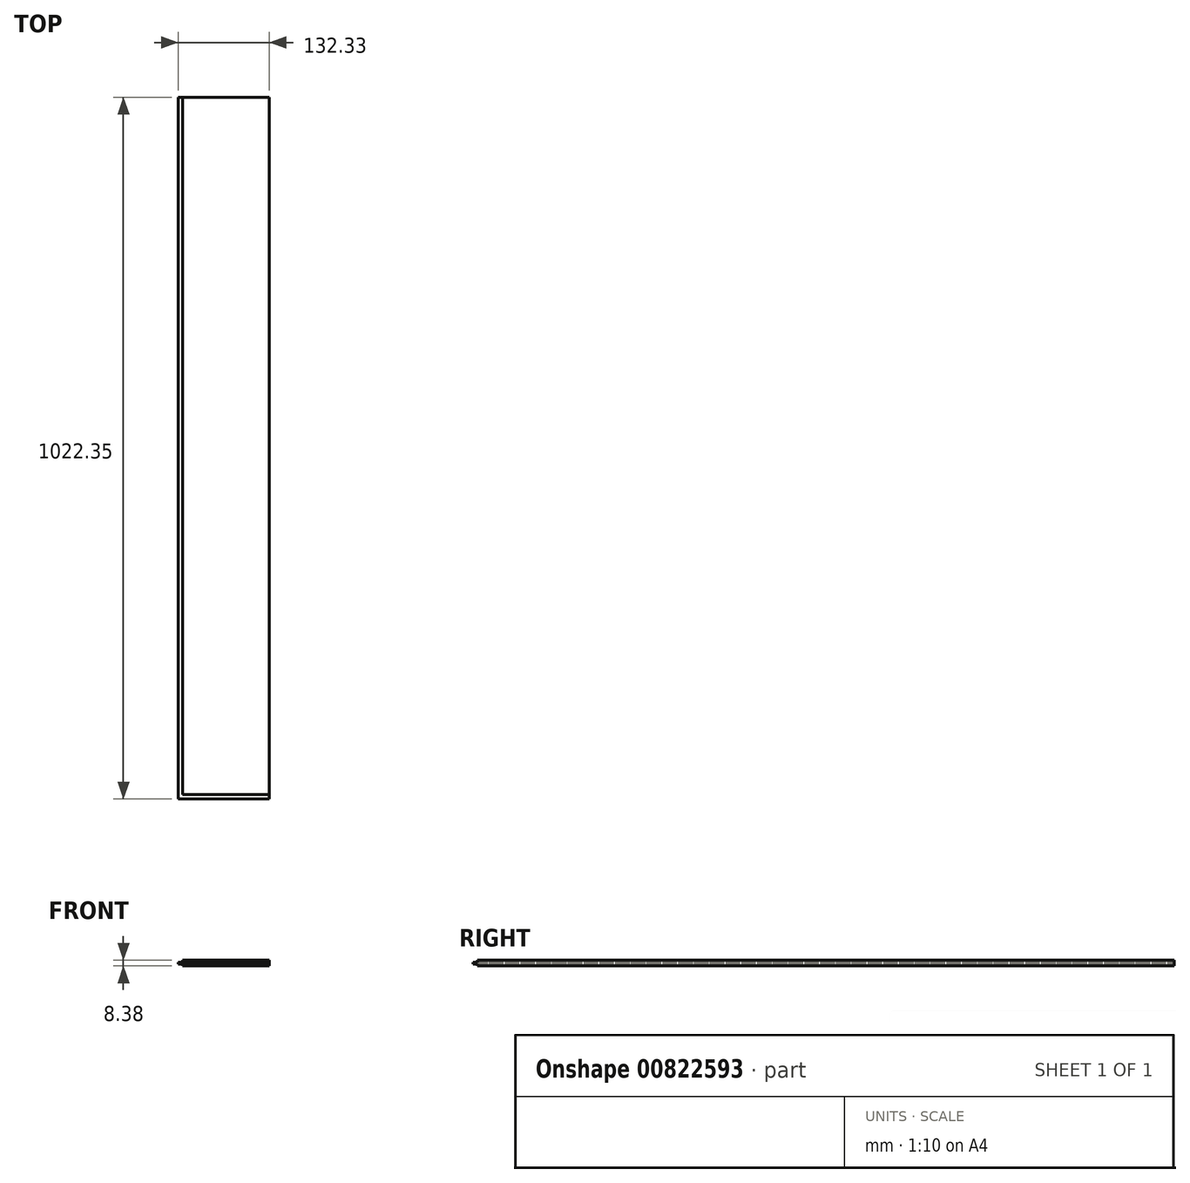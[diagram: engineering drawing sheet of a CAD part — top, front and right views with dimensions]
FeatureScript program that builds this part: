
annotation { "Feature Type Name" : "Feature", "Feature Type Description" : "" }
export const myFeature = defineFeature(function(context is Context, id is Id, definition is map)
    precondition{}
    {
        {
            var Q0;
            Q0=qCreatedBy(makeId("Front.planeOp"),FACE);
            var sketch = newSketch(context, id + "F0", { "sketchPlane" : qUnion([Q0])});
            skLineSegment(sketch, "E0.bottom", {"start": v(0, 0) * mm, "end": v(125.98, 0) * mm});
            skLineSegment(sketch, "E0.top", {"start": v(0, -8.38) * mm, "end": v(125.98, -8.38) * mm});
            skLineSegment(sketch, "E0.left", {"start": v(0, 0) * mm, "end": v(0, -8.38) * mm});
            skLineSegment(sketch, "E0.right", {"start": v(125.98, 0) * mm, "end": v(125.98, -8.38) * mm});
            skSolve(sketch);
        }
        {
            var Q0;
            Q0=qSketchRegion(id+"F0",true);
            extrude(context, id + "F1", {"entities" : qUnion([Q0]), "depth" : 1290.07 * mm, "offsetDistance" : 25.4 * mm});
        }
        {
            var Q0;
            Q0=makeQuery(id+"F0.imprint","IMPRINT",FACE,{"disambiguationData":[TD([[makeQuery(id+"F0.imprint","IMPRINT",EDGE,{"derivedFrom":sQuery(id+"F0.wireOp",EDGE,"E0.bottom")}),-1.0]])]});
            var sketch = newSketch(context, id + "F2", { "sketchPlane" : qUnion([Q0])});
            skLineSegment(sketch, "E1.bottom", {"start": v(0, -2.8) * mm, "end": v(-6.35, -2.8) * mm});
            skLineSegment(sketch, "E1.top", {"start": v(0, -5.59) * mm, "end": v(-6.35, -5.59) * mm});
            skLineSegment(sketch, "E1.left", {"start": v(0, -2.8) * mm, "end": v(0, -5.59) * mm});
            skLineSegment(sketch, "E1.right", {"start": v(-6.35, -2.8) * mm, "end": v(-6.35, -5.59) * mm});
            skSolve(sketch);
        }
        {
            var Q0;
            Q0=makeQuery(id+"F2.imprint","IMPRINT",FACE,{"disambiguationData":[TD([[makeQuery(id+"F2.imprint","IMPRINT",EDGE,{"derivedFrom":sQuery(id+"F2.wireOp",EDGE,"E1.bottom")}),1.0]])]});
            extrude(context, id + "F3", {"entities" : qUnion([Q0]), "operationType" : NewBodyOperationType.ADD, "endBound" : BoundingType.THROUGH_ALL, "depth" : 25.4 * mm, "offsetDistance" : 25.4 * mm});
        }
        {
            var Q0;
            Q0=makeQuery(id+"F3.opExtrude","SWEPT_FACE",FACE,{"disambiguationData":[OSD([sQuery(id+"F2.wireOp",EDGE,"E1.right")])]});
            var sketch = newSketch(context, id + "F4", { "sketchPlane" : qUnion([Q0])});
            skLineSegment(sketch, "E2.bottom", {"start": v(1296.87, -2.8) * mm, "end": v(1296.42, -2.8) * mm});
            skLineSegment(sketch, "E2.top", {"start": v(1296.87, -5.59) * mm, "end": v(1296.42, -5.59) * mm});
            skLineSegment(sketch, "E2.left", {"start": v(1296.87, -2.8) * mm, "end": v(1296.87, -5.59) * mm});
            skLineSegment(sketch, "E2.right", {"start": v(1296.42, -2.8) * mm, "end": v(1296.42, -5.59) * mm});
            skSolve(sketch);
        }
        {
            var Q0;
            Q0=qSketchRegion(id+"F4",true);
            extrude(context, id + "F5", {"entities" : qUnion([Q0]), "operationType" : NewBodyOperationType.REMOVE, "endBound" : BoundingType.THROUGH_ALL, "oppositeDirection" : true, "depth" : 25.4 * mm, "offsetDistance" : 25.4 * mm});
        }
        {
            var Q0;
            Q0=makeQuery(id+"F3.opExtrude","SWEPT_FACE",FACE,{"disambiguationData":[OSD([sQuery(id+"F2.wireOp",EDGE,"E1.right")])]});
            var sketch = newSketch(context, id + "F6", { "sketchPlane" : qUnion([Q0])});
            skLineSegment(sketch, "E3.bottom", {"start": v(1296.42, -2.8) * mm, "end": v(1290.07, -2.8) * mm});
            skLineSegment(sketch, "E3.top", {"start": v(1296.42, -5.59) * mm, "end": v(1290.07, -5.59) * mm});
            skLineSegment(sketch, "E3.left", {"start": v(1296.42, -2.8) * mm, "end": v(1296.42, -5.59) * mm});
            skLineSegment(sketch, "E3.right", {"start": v(1290.07, -2.8) * mm, "end": v(1290.07, -5.59) * mm});
            skSolve(sketch);
        }
        {
            var Q0;
            Q0=qSketchRegion(id+"F6",true);
            var Q1;
            Q1=makeQuery(id+"F1.opExtrude","SWEPT_FACE",FACE,{"disambiguationData":[OSD([sQuery(id+"F0.wireOp",EDGE,"E0.right")])]});
            extrude(context, id + "F7", {"entities" : qUnion([Q0]), "operationType" : NewBodyOperationType.ADD, "endBound" : BoundingType.UP_TO_SURFACE, "oppositeDirection" : true, "depth" : 25.4 * mm, "endBoundEntityFace" : qUnion([Q1]), "offsetDistance" : 25.4 * mm});
        }
        {
            var Q0;
            Q0=makeQuery(id+"F3.boolean.opBoolean","MERGE",FACE,{"derivedFrom":[makeQuery(id+"F1.opExtrude","CAP_FACE",FACE,{"disambiguationData":[OSD([sQuery(id+"F0.wireOp",EDGE,"E0.bottom"),sQuery(id+"F0.wireOp",EDGE,"E0.top"),sQuery(id+"F0.wireOp",EDGE,"E0.left"),sQuery(id+"F0.wireOp",EDGE,"E0.right")])],"isStart":true}),makeQuery(id+"F3.opExtrude","CAP_FACE",FACE,{"disambiguationData":[OSD([sQuery(id+"F2.wireOp",EDGE,"E1.bottom"),sQuery(id+"F2.wireOp",EDGE,"E1.top"),sQuery(id+"F2.wireOp",EDGE,"E1.left"),sQuery(id+"F2.wireOp",EDGE,"E1.right")])],"isStart":true})]});
            var sketch = newSketch(context, id + "F8", { "sketchPlane" : qUnion([Q0])});
            skLineSegment(sketch, "E4.bottom", {"start": v(6.35, -2.8) * mm, "end": v(-125.98, -2.8) * mm});
            skLineSegment(sketch, "E4.top", {"start": v(6.35, -5.59) * mm, "end": v(-125.98, -5.59) * mm});
            skLineSegment(sketch, "E4.left", {"start": v(6.35, -2.8) * mm, "end": v(6.35, -5.59) * mm});
            skLineSegment(sketch, "E4.right", {"start": v(-125.98, -2.8) * mm, "end": v(-125.98, -5.59) * mm});
            skSolve(sketch);
        }
        {
            var Q0;
            {var subQ0=sQuery(id+"F8.wireOp",EDGE,"E4.left");Q0=makeQuery(id+"F8.imprint","IMPRINT",FACE,{"disambiguationData":[TD([[makeQuery(id+"F8.imprint","IMPRINT",EDGE,{"derivedFrom":subQ0}),-1.0]])]});}
            extrude(context, id + "F9", {"entities" : qUnion([Q0]), "operationType" : NewBodyOperationType.REMOVE, "oppositeDirection" : true, "depth" : 6.35 * mm, "offsetDistance" : 25.4 * mm});
        }
        {
            var Q0;
            Q0=makeQuery(id+"F1.opExtrude","SWEPT_FACE",FACE,{"disambiguationData":[OSD([sQuery(id+"F0.wireOp",EDGE,"E0.bottom")])]});
            var sketch = newSketch(context, id + "F10", { "sketchPlane" : qUnion([Q0])});
            skLineSegment(sketch, "E5.bottom", {"start": v(125.98, 0) * mm, "end": v(-932.72, 0) * mm});
            skLineSegment(sketch, "E5.top", {"start": v(125.98, -274.07) * mm, "end": v(-932.72, -274.07) * mm});
            skLineSegment(sketch, "E5.left", {"start": v(125.98, 0) * mm, "end": v(125.98, -274.07) * mm});
            skLineSegment(sketch, "E5.right", {"start": v(-932.72, 0) * mm, "end": v(-932.72, -274.07) * mm});
            skSolve(sketch);
        }
        {
            var Q0;
            {var subQ4=sQuery(id+"F10.wireOp",EDGE,"E5.left");Q0=makeQuery(id+"F10.imprint","IMPRINT",FACE,{"disambiguationData":[TD([[makeQuery(id+"F10.imprint","IMPRINT",EDGE,{"derivedFrom":subQ4}),1.0]])]});}
            var Q1;
            {var subQ3=sQuery(id+"F10.wireOp",EDGE,"E5.right");Q1=makeQuery(id+"F10.imprint","IMPRINT",FACE,{"disambiguationData":[TD([[makeQuery(id+"F10.imprint","IMPRINT",EDGE,{"derivedFrom":subQ3}),1.0]])]});}
            extrude(context, id + "F11", {"entities" : qUnion([Q0, Q1]), "operationType" : NewBodyOperationType.REMOVE, "oppositeDirection" : true, "depth" : 25.4 * mm, "offsetDistance" : 25.4 * mm});
        }
        {
            var Q0;
            Q0=makeQuery(id+"F1.opExtrude","SWEPT_BODY",BODY,{"disambiguationData":[OSD([sQuery(id+"F0.wireOp",EDGE,"E0.bottom"),sQuery(id+"F0.wireOp",EDGE,"E0.top"),sQuery(id+"F0.wireOp",EDGE,"E0.left"),sQuery(id+"F0.wireOp",EDGE,"E0.right")])]});
            transform(context, id + "F12", {"entities" : qUnion([Q0]), "transformType" : TransformType.TRANSLATION_3D, "dx" : 0 * mm, "dy" : 0 * mm, "dz" : 0 * mm, "makeCopy" : true});
        }
    });
